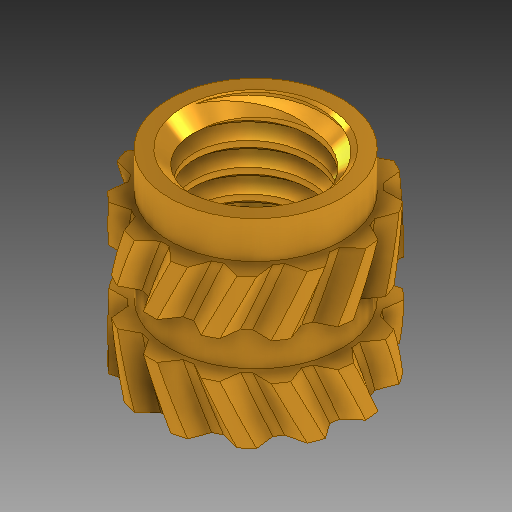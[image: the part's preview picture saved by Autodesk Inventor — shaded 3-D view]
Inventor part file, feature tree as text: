
AUTODESK INVENTOR PART (.ipt)
format: ipt  version: 2020 (Build 240168000, 168)  size: 745,472 bytes
history: native  units: mm
features: other x1, thread x1
ambient origin geometry x8: Origin, YZ Plane, XZ Plane, XY Plane, X Axis, Y Axis, Z Axis, Center Point
bodies: Body1 (feature_tree)
feature tree (2):
  other  "Твердое тело1"
  thread  "Thread2"  [1 undecoded]
note: 1 required parameter value undecoded (feature->parameter linkage not recoverable at this tier; creation-order binding heuristic only, values carry confidence <= 0.55)
